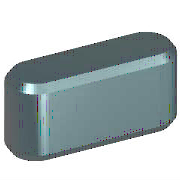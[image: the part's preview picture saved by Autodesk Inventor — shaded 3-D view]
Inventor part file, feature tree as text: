
AUTODESK INVENTOR PART (.ipt)
format: ipt  version: 2025 (Build 290162000, 162)  size: 137,216 bytes
history: native  units: mm (DEFAULTED — no unit token found)
features: plane x3, extrude x1
ambient origin geometry x8: Origin, YZ Plane, XZ Plane, XY Plane, X Axis, Y Axis, Z Axis, Center Point
bodies: Solid1 (feature_tree)
feature tree (4):
  plane  "Work Plane1"
  plane  "Work Plane2"
  extrude  "轴承体1"  Depth=3.0mm
  plane  "Work Plane3"
